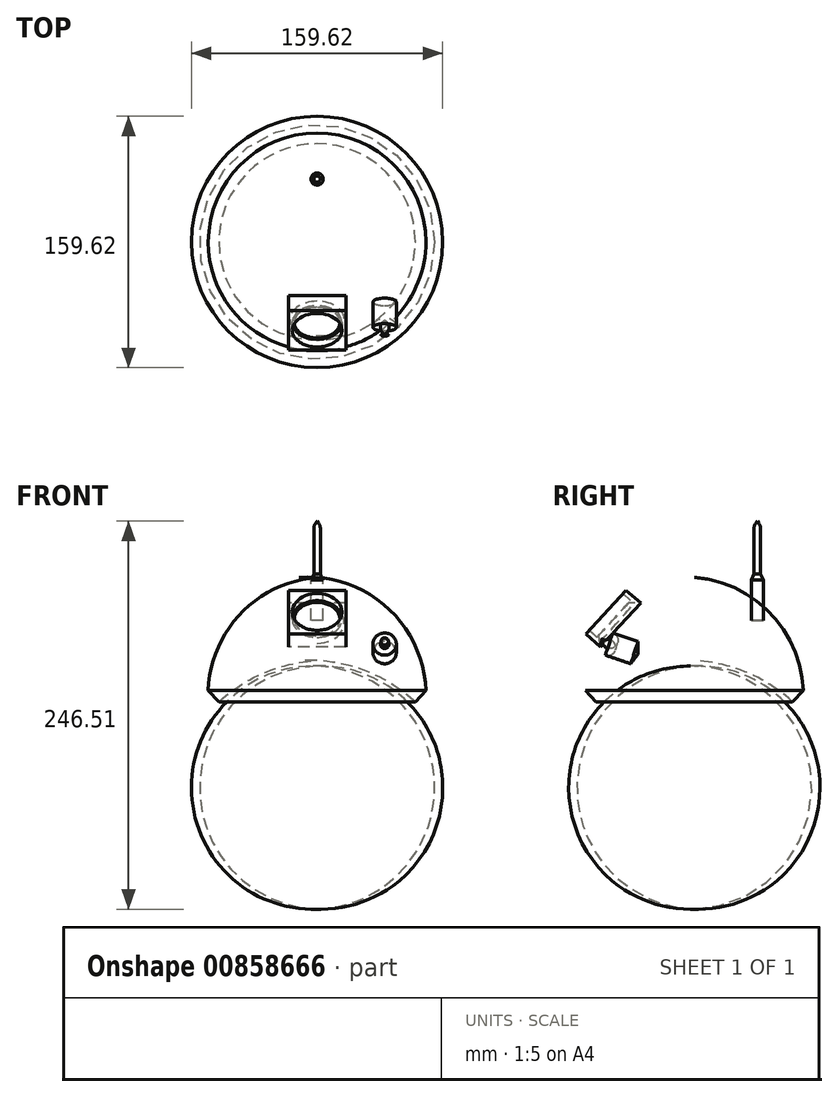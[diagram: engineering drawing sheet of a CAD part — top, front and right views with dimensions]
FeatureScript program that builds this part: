
annotation { "Feature Type Name" : "Feature", "Feature Type Description" : "" }
export const myFeature = defineFeature(function(context is Context, id is Id, definition is map)
    precondition{}
    {
        {
            var Q0;
            Q0=qCreatedBy(makeId("Front.planeOp"),FACE);
            var sketch = newSketch(context, id + "F0", { "sketchPlane" : qUnion([Q0])});
            skArc(sketch, "E0", {"start": v(0, -77.3) * mm, "mid": v(79.8, -0.14) * mm, "end": v(0, 77.02) * mm});
            skLineSegment(sketch, "E1", {"start": v(0, -77.3) * mm, "end": v(0, 77.02) * mm});
            skSolve(sketch);
        }
        {
            var Q0;
            Q0 = qSketchRegion(id + "F0", true);
            var Q1;
            Q1=sQuery(id+"F0.wireOp",EDGE,"E1");
            revolve(context, id + "F1", {"surfaceOperationType" : NewSurfaceOperationType.NEW, "entities" : qUnion([Q0]), "axis" : qUnion([Q1]), "revolveType" : RevolveType.FULL});
        }
        {
            var Q0;
            Q0=qCreatedBy(makeId("Front.planeOp"),FACE);
            var sketch = newSketch(context, id + "F2", { "sketchPlane" : qUnion([Q0])});
            skLineSegment(sketch, "E2", {"start": v(-62.35, 54.38) * mm, "end": v(-69.12, 61.6) * mm});
            skArc(sketch, "E3", {"start": v(0, 133.37) * mm, "mid": v(-48.23, 110.65) * mm, "end": v(-69.12, 61.6) * mm});
            skArc(sketch, "E4", {"start": v(0, 80.56) * mm, "mid": v(-33.44, 72.87) * mm, "end": v(-62.35, 54.38) * mm});
            skLineSegment(sketch, "E5", {"start": v(0, 80.56) * mm, "end": v(0, 133.37) * mm});
            skSolve(sketch);
        }
        {
            var Q0;
            Q0 = qSketchRegion(id + "F2", true);
            var Q1;
            Q1=sQuery(id+"F2.wireOp",EDGE,"E5");
            revolve(context, id + "F3", {"surfaceOperationType" : NewSurfaceOperationType.NEW, "entities" : qUnion([Q0]), "axis" : qUnion([Q1]), "revolveType" : RevolveType.FULL});
        }
        {
            var Q0;
            Q0=qCreatedBy(makeId("Right.planeOp"),FACE);
            var sketch = newSketch(context, id + "F4", { "sketchPlane" : qUnion([Q0])});
            skFitSpline(sketch, "E6", {"points": [v(-43.1, 117.58) * mm, v(-50.6, 113.64) * mm, v(-55.31, 110.1) * mm, v(-56.1, 109.7) * mm], "startDerivative": vector(-16.58, -7.6) * mm, "endDerivative": vector(-4.35, -1.62) * mm});
            skLineSegment(sketch, "E7", {"start": v(-55.31, 110.1) * mm, "end": v(-49.02, 104.59) * mm});
            skLineSegment(sketch, "E8", {"start": v(-49.02, 104.59) * mm, "end": v(-37.65, 117.58) * mm});
            skLineSegment(sketch, "E9", {"start": v(-37.65, 117.58) * mm, "end": v(-43.1, 117.58) * mm});
            skSolve(sketch);
        }
        {
            var Q0;
            Q0 = qSketchRegion(id + "F4", true);
            var Q1;
            Q1=sQuery(id+"F4.wireOp",EDGE,"E7");
            revolve(context, id + "F5", {"surfaceOperationType" : NewSurfaceOperationType.NEW, "entities" : qUnion([Q0]), "axis" : qUnion([Q1]), "revolveType" : RevolveType.FULL});
        }
        {
            var Q0;
            Q0=qCreatedBy(makeId("Right.planeOp"),FACE);
            var sketch = newSketch(context, id + "F6", { "sketchPlane" : qUnion([Q0])});
            skLineSegment(sketch, "E10", {"start": v(-34.05, 117.18) * mm, "end": v(-59.65, 89.23) * mm});
            skLineSegment(sketch, "E11", {"start": v(-59.65, 89.23) * mm, "end": v(-68.74, 97.56) * mm});
            skLineSegment(sketch, "E12", {"start": v(-68.74, 97.56) * mm, "end": v(-43.5, 125.13) * mm});
            skLineSegment(sketch, "E13", {"start": v(-43.5, 125.13) * mm, "end": v(-34.05, 117.18) * mm});
            skSolve(sketch);
        }
        {
            var Q0;
            Q0 = qSketchRegion(id + "F6", true);
            extrude(context, id + "F7", {"entities" : qUnion([Q0]), "endBound" : BoundingType.SYMMETRIC, "depth" : 36.58 * mm, "offsetDistance" : 25.4 * mm});
        }
        {
            var Q0;
            Q0=makeQuery(id+"F7.opExtrude","SWEPT_FACE",FACE,{"disambiguationData":[OSD([sQuery(id+"F6.wireOp",EDGE,"E12")])]});
            var sketch = newSketch(context, id + "F8", { "sketchPlane" : qUnion([Q0])});
            skCircle(sketch, "E14", {"center": v(0, 44.37) * mm, "radius": 15.8 * mm});
            skSolve(sketch);
        }
        {
            var Q0;
            Q0 = qSketchRegion(id + "F8", true);
            extrude(context, id + "F9", {"entities" : qUnion([Q0]), "operationType" : NewBodyOperationType.REMOVE, "oppositeDirection" : true, "depth" : 6.6 * mm, "offsetDistance" : 25.4 * mm});
        }
        {
            var Q0;
            Q0=qCreatedBy(makeId("Right.planeOp"),FACE);
            var sketch = newSketch(context, id + "F10", { "sketchPlane" : qUnion([Q0])});
            skLineSegment(sketch, "E15", {"start": v(43.78, 106.1) * mm, "end": v(43.78, 131.63) * mm});
            skLineSegment(sketch, "E16", {"start": v(43.78, 131.63) * mm, "end": v(42, 135.46) * mm});
            skLineSegment(sketch, "E17", {"start": v(42, 135.46) * mm, "end": v(42, 166.35) * mm});
            skLineSegment(sketch, "E18", {"start": v(42, 166.35) * mm, "end": v(39.95, 169.16) * mm});
            skLineSegment(sketch, "E19", {"start": v(39.95, 169.16) * mm, "end": v(39.95, 106.1) * mm});
            skLineSegment(sketch, "E20", {"start": v(39.95, 106.1) * mm, "end": v(43.78, 106.1) * mm});
            skSolve(sketch);
        }
        {
            var Q0;
            Q0 = qSketchRegion(id + "F10", true);
            var Q1;
            Q1=sQuery(id+"F10.wireOp",EDGE,"E19");
            revolve(context, id + "F11", {"surfaceOperationType" : NewSurfaceOperationType.NEW, "entities" : qUnion([Q0]), "axis" : qUnion([Q1]), "revolveType" : RevolveType.FULL});
        }
        {
            var Q0;
            Q0=qCreatedBy(makeId("Right.planeOp"),FACE);
            cPlane(context, id + "F12", {"entities" : qUnion([Q0]), "cplaneType" : CPlaneType.OFFSET, "offset" : 42.93 * mm, "width" : 152.4 * mm, "height" : 152.4 * mm});
        }
        {
            var Q0;
            Q0=qCreatedBy(id+"F12.planeOp",FACE);
            var sketch = newSketch(context, id + "F13", { "sketchPlane" : qUnion([Q0])});
            skLineSegment(sketch, "E21", {"start": v(-35.7, 92.65) * mm, "end": v(-56.7, 99.69) * mm});
            skLineSegment(sketch, "E22", {"start": v(-56.7, 99.69) * mm, "end": v(-59.05, 92.65) * mm});
            skLineSegment(sketch, "E23", {"start": v(-59.05, 92.65) * mm, "end": v(-35.7, 84.82) * mm});
            skLineSegment(sketch, "E24", {"start": v(-35.7, 84.82) * mm, "end": v(-35.7, 92.65) * mm});
            skSolve(sketch);
        }
        {
            var Q0;
            Q0=makeQuery(id+"F13.imprint","IMPRINT",FACE,{"disambiguationData":[TD([[makeQuery(id+"F13.imprint","IMPRINT",EDGE,{"derivedFrom":sQuery(id+"F13.wireOp",EDGE,"E21")}),1.0]])]});
            var Q1;
            Q1=sQuery(id+"F13.wireOp",EDGE,"E23");
            revolve(context, id + "F14", {"surfaceOperationType" : NewSurfaceOperationType.NEW, "entities" : qUnion([Q0]), "axis" : qUnion([Q1]), "revolveType" : RevolveType.FULL});
        }
        {
            var Q0;
            Q0=makeQuery(id+"F14.opRevolve","SWEPT_EDGE",EDGE,{"disambiguationData":[OSD([sQuery(id+"F13.wireOp",EDGE,"E21"),sQuery(id+"F13.wireOp",EDGE,"E22")])]});
            fillet(context, id + "F15", {"entities" : qUnion([Q0]), "radius" : 5.08 * mm, "tangentPropagation" : true, "allowEdgeOverflow" : false});
        }
        {
            var Q0;
            Q0=makeQuery(id+"F11.opRevolve","SWEPT_EDGE",EDGE,{"disambiguationData":[OSD([sQuery(id+"F10.wireOp",EDGE,"E17"),sQuery(id+"F10.wireOp",EDGE,"E18")])]});
            fillet(context, id + "F16", {"entities" : qUnion([Q0]), "radius" : 5.08 * mm, "tangentPropagation" : true, "allowEdgeOverflow" : false});
        }
    });
